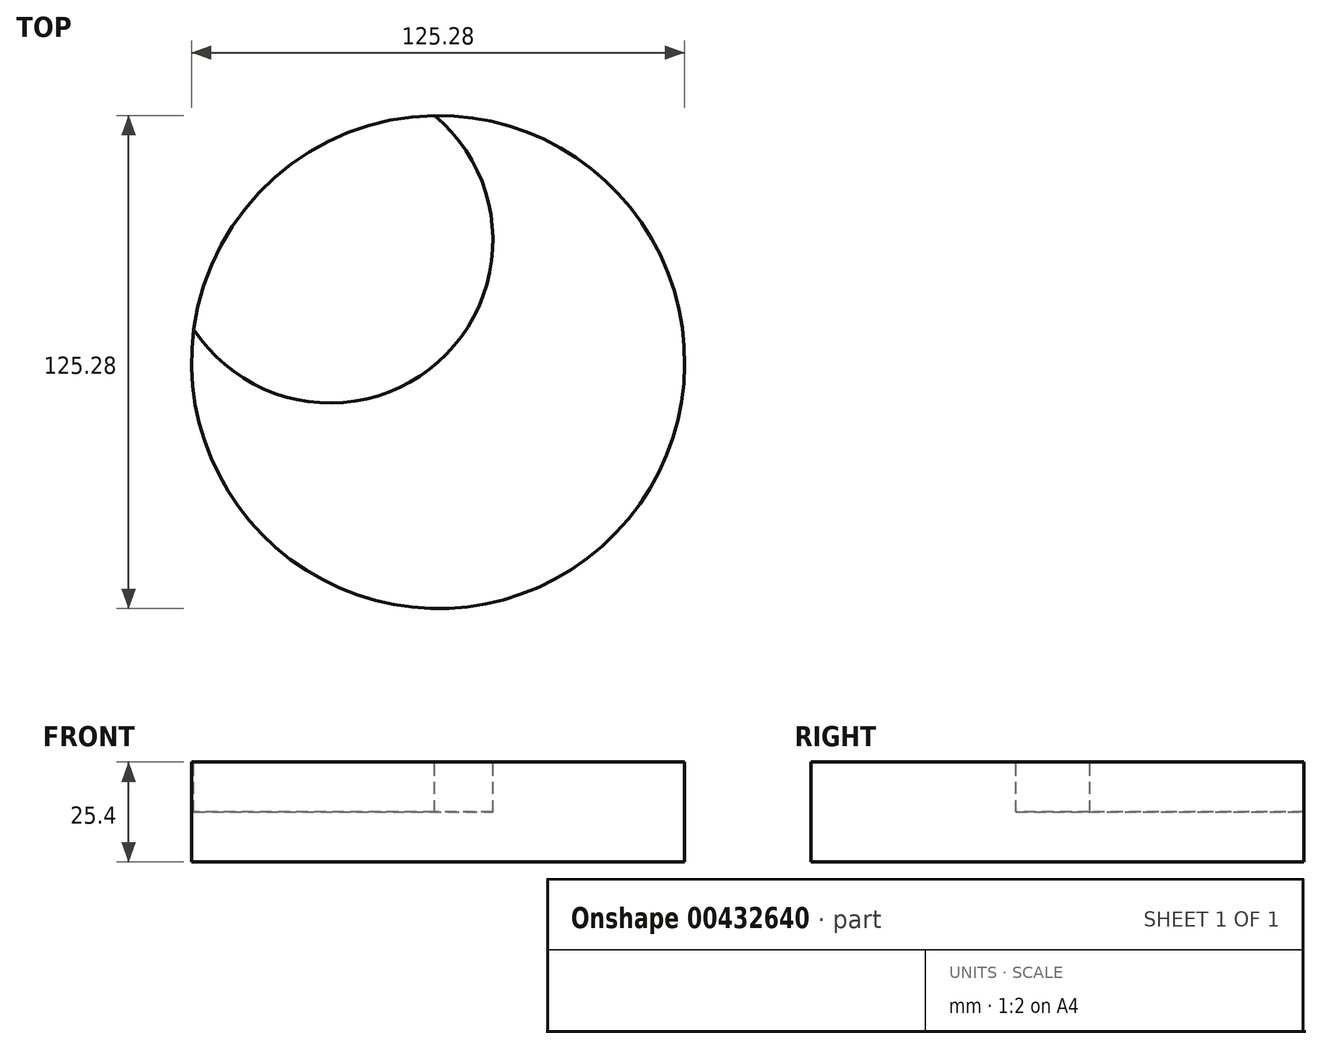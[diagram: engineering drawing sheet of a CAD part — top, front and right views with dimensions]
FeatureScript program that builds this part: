
annotation { "Feature Type Name" : "Feature", "Feature Type Description" : "" }
export const myFeature = defineFeature(function(context is Context, id is Id, definition is map)
    precondition{}
    {
        {
            var Q0;
            Q0=qCreatedBy(makeId("Top.planeOp"),FACE);
            var sketch = newSketch(context, id + "F0", { "sketchPlane" : qUnion([Q0])});
            skCircle(sketch, "E0", {"center": v(0, 0) * mm, "radius": 62.64 * mm});
            skSolve(sketch);
        }
        {
            var Q0;
            Q0=makeQuery(id+"F0.imprint","IMPRINT",FACE,{"disambiguationData":[TD([[makeQuery(id+"F0.imprint","IMPRINT",EDGE,{"derivedFrom":sQuery(id+"F0.wireOp",EDGE,"E0")}),1.0]])]});
            var Q1;
            Q1=sQuery(id+"F0.wireOp",EDGE,"E0");
            extrude(context, id + "F1", {"entities" : qUnion([Q0]), "surfaceEntities" : qUnion([Q1]), "endBound" : BoundingType.SYMMETRIC, "depth" : 25.4 * mm});
        }
        {
            var Q0;
            Q0=makeQuery(id+"F1.opExtrude","CAP_FACE",FACE,{"disambiguationData":[OSD([sQuery(id+"F0.wireOp",EDGE,"E0")])],"isStart":false});
            var sketch = newSketch(context, id + "F2", { "sketchPlane" : qUnion([Q0])});
            skCircle(sketch, "E1", {"center": v(-27.47, 30.93) * mm, "radius": 41.37 * mm});
            skSolve(sketch);
        }
        {
            var Q0;
            {var subQ0=sQuery(id+"F2.wireOp",EDGE,"E1");var subQ1=makeQuery(id+"F1.opExtrude","CAP_EDGE",EDGE,{"disambiguationData":[OSD([sQuery(id+"F0.wireOp",EDGE,"E0")])],"isStart":false});var subQ2=makeQuery(id+"F2.imprint","INTERSECT",VERTEX,{"disambiguationData":[OD(0.0)],"derivedFrom":[subQ1,subQ0]});Q0=makeQuery(id+"F2.imprint","IMPRINT",FACE,{"disambiguationData":[TD([[makeQuery(id+"F2.imprint","IMPRINT",EDGE,{"disambiguationData":[TD([[subQ2,1.0]])],"derivedFrom":subQ0}),1.0]])]});}
            var Q1;
            {var subQ0=sQuery(id+"F2.wireOp",EDGE,"E1");var subQ1=makeQuery(id+"F1.opExtrude","CAP_EDGE",EDGE,{"disambiguationData":[OSD([sQuery(id+"F0.wireOp",EDGE,"E0")])],"isStart":false});var subQ2=makeQuery(id+"F2.imprint","INTERSECT",VERTEX,{"disambiguationData":[OD(0.0)],"derivedFrom":[subQ1,subQ0]});Q1=makeQuery(id+"F2.imprint","IMPRINT",FACE,{"disambiguationData":[TD([[makeQuery(id+"F2.imprint","IMPRINT",EDGE,{"disambiguationData":[TD([[subQ2,-1.0]])],"derivedFrom":subQ0}),1.0]])]});}
            var Q2;
            Q2=sQuery(id+"F2.wireOp",EDGE,"E1");
            extrude(context, id + "F3", {"entities" : qUnion([Q0, Q1]), "operationType" : NewBodyOperationType.REMOVE, "surfaceEntities" : qUnion([Q2]), "endBound" : BoundingType.SYMMETRIC, "oppositeDirection" : true, "depth" : 25.4 * mm});
        }
    });
